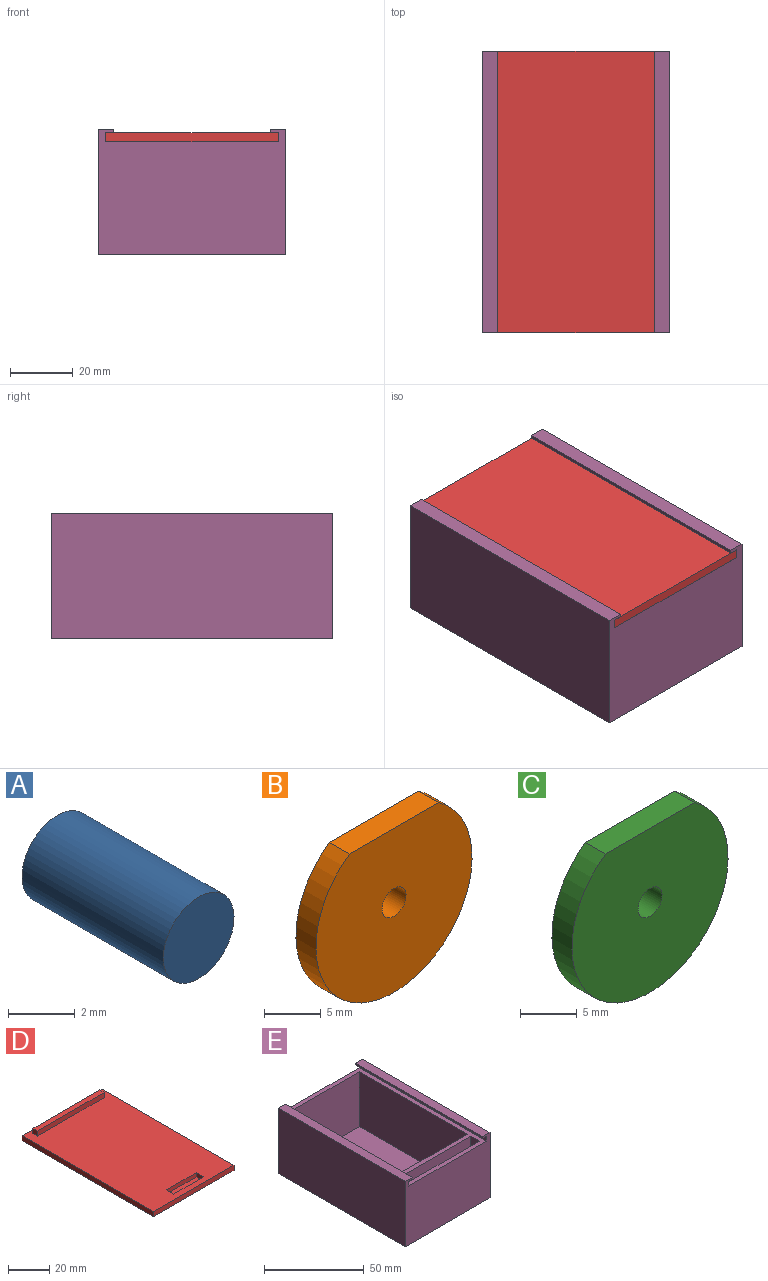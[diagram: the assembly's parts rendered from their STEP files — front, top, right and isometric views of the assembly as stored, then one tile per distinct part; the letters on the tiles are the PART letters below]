
ASSEMBLY  parts=5 mates=4
PART A: 3 faces, bbox 3x6x3 mm
  f0: cylinder r=1.5mm len=6mm, axis (0,1,0), area 56.5mm2, adj f1,f2
  f1: plane 3x3mm, normal (0,-1,0), area 7.1mm2, adj f0
  f2: plane 3x3mm, normal (0,1,0), area 7.1mm2, adj f0
PART B: 5 faces, bbox 19.5x2.5x17.8 mm
  f0: plane 11.15x2.5mm, normal (0,0,1), area 27.9mm2, adj f2,f3,f4
  f1: cylinder r=1.5mm len=3mm, axis (0,1,0), area 23.6mm2, adj f3,f4
  f2: cylinder r=9.75mm len=19.5mm, axis (0,1,0), area 123.5mm2, adj f0,f3,f4
  f3: plane 19.5x17.75mm, normal (0,-1,0), area 278.3mm2, adj f0,f1,f2
  f4: plane 19.5x17.75mm, normal (0,1,0), area 278.3mm2, adj f0,f1,f2
PART C: 5 faces, bbox 19.5x2.5x17.8 mm
  f0: plane 11.15x2.5mm, normal (0,0,1), area 27.9mm2, adj f2,f3,f4
  f1: cylinder r=1.5mm len=3mm, axis (0,1,0), area 23.6mm2, adj f3,f4
  f2: cylinder r=9.75mm len=19.5mm, axis (0,1,0), area 123.5mm2, adj f0,f3,f4
  f3: plane 19.5x17.75mm, normal (0,-1,0), area 278.3mm2, adj f0,f1,f2
  f4: plane 19.5x17.75mm, normal (0,1,0), area 278.3mm2, adj f0,f1,f2
PART D: 16 faces, bbox 55x90x6 mm
  f0: plane 90x55mm, normal (0,0,1), area 4710.4mm2, adj f1,f2,f3,f5,f6,f7,f8,f9
  f1: plane 55x3mm, normal (0,1,0), area 165mm2, adj f0,f2,f4,f5
  f2: plane 90x3mm, normal (-1,0,0), area 270mm2, adj f0,f1,f3,f4
  f3: plane 55x3mm, normal (0,-1,0), area 165mm2, adj f0,f2,f4,f5
  f4: plane 90x55mm, normal (0,0,-1), area 4950mm2, adj f1,f2,f3,f5
  f5: plane 90x3mm, normal (1,0,0), area 270mm2, adj f0,f1,f3,f4
  f6: plane 20.5x2.5mm, normal (0,-1,0), area 51.2mm2, adj f0,f7,f9,f10
  f7: plane 5x2.5mm, normal (1,0,0), area 12.5mm2, adj f0,f6,f8,f10
  f8: plane 20.5x2.5mm, normal (0,1,0), area 51.2mm2, adj f0,f7,f9,f10
  f9: plane 5x2.5mm, normal (-1,0,0), area 12.5mm2, adj f0,f6,f8,f10
  f10: plane 20.5x5mm, normal (0,0,1), area 102.5mm2, adj f6,f7,f8,f9
  f11: plane 45.71x3mm, normal (0,1,0), area 137.1mm2, adj f0,f12,f14,f15
  f12: plane 3x3mm, normal (-1,0,0), area 9mm2, adj f0,f11,f13,f15
  f13: plane 45.71x3mm, normal (0,-1,0), area 137.1mm2, adj f0,f12,f14,f15
  f14: plane 3x3mm, normal (1,0,0), area 9mm2, adj f0,f11,f13,f15
  f15: plane 45.71x3mm, normal (0,0,1), area 137.1mm2, adj f11,f12,f13,f14
PART E: 24 faces, bbox 60x90x40 mm
  f0: plane 50x6mm, normal (0,0,1), area 300mm2, adj f2,f18,f21,f23
  f1: plane 76.5x33.5mm, normal (1,0,0), area 2562.7mm2, adj f16,f17,f19,f22
  f2: plane 33.5x6mm, normal (-1,0,0), area 201mm2, adj f0,f16,f21,f23
  f3: plane 90x5mm, normal (0,0,1), area 450mm2, adj f4,f6,f7,f8
  f4: plane 90x1mm, normal (-1,0,0), area 90mm2, adj f3,f6,f8,f15
  f5: plane 90x1mm, normal (1,0,0), area 90mm2, adj f6,f8,f10,f12
  f6: plane 60x40mm, normal (0,-1,0), area 2185mm2, adj f3,f4,f5,f7,f9,f10,f11,f12
  f7: plane 90x40mm, normal (1,0,0), area 3600mm2, adj f3,f6,f8,f11
  f8: plane 60x40mm, normal (0,1,0), area 2185mm2, adj f3,f4,f5,f7,f9,f10,f11,f12
  f9: plane 90x40mm, normal (-1,0,0), area 3600mm2, adj f6,f8,f10,f11
  f10: plane 90x5mm, normal (0,0,1), area 450mm2, adj f5,f6,f8,f9
  f11: plane 90x60mm, normal (0,0,-1), area 5400mm2, adj f6,f7,f8,f9
  f12: plane 90x2.5mm, normal (0,0,-1), area 225mm2, adj f5,f6,f8,f13
  f13: plane 90x3mm, normal (1,0,0), area 270mm2, adj f6,f8,f12,f16
  f14: plane 90x3mm, normal (-1,0,0), area 270mm2, adj f6,f8,f15,f16
  f15: plane 90x2.5mm, normal (0,0,-1), area 225mm2, adj f4,f6,f8,f14
  f16: plane 90x55mm, normal (0,0,1), area 825mm2, adj f1,f2,f6,f8,f13,f14,f18,f19
  f17: plane 76.5x50mm, normal (0,0,1), area 3825mm2, adj f1,f19,f20,f22
  f18: plane 33.5x6mm, normal (1,0,0), area 201mm2, adj f0,f16,f21,f23
  f19: plane 50x33.5mm, normal (0,-1,0), area 1675mm2, adj f1,f16,f17,f20
  f20: plane 76.5x33.5mm, normal (-1,0,0), area 2562.7mm2, adj f16,f17,f19,f22
  f21: plane 50x33.5mm, normal (0,1,0), area 1675mm2, adj f0,f2,f16,f18
  f22: plane 50x33.5mm, normal (0,1,0), area 1675mm2, adj f1,f16,f17,f20
  f23: plane 50x33.5mm, normal (0,-1,0), area 1675mm2, adj f0,f2,f16,f18
PLACE A t=(13.12,-8.91,36.63)mm
PLACE B rot(axis=(0,1,0),1.7deg) t=(12.25,-8.91,35.73)mm
PLACE C rot(axis=(0,-1,0),33.1deg) t=(23.54,-8.91,57.53)mm
PLACE D rot(axis=(0,1,0),180deg) t=(10.62,-8.91,75.62)mm
PLACE E t=(13.12,-8.91,36.63)mm fixed
MATE revolute B.f1 <-> C.f1  axis (0,1,0) through (-16.88,-2.91,64.63)mm
MATE slider D.f3 <-> E.f6  axis (0,-1,0) through (-16.88,-8.91,74.12)mm
MATE revolute C.f1 <-> A.f0  axis (0,1,0) through (-16.88,-0.41,64.63)mm
MATE fastened E.f23 <-> A.f2  axis (0,-1,0) through (-16.88,-0.41,55.88)mm
